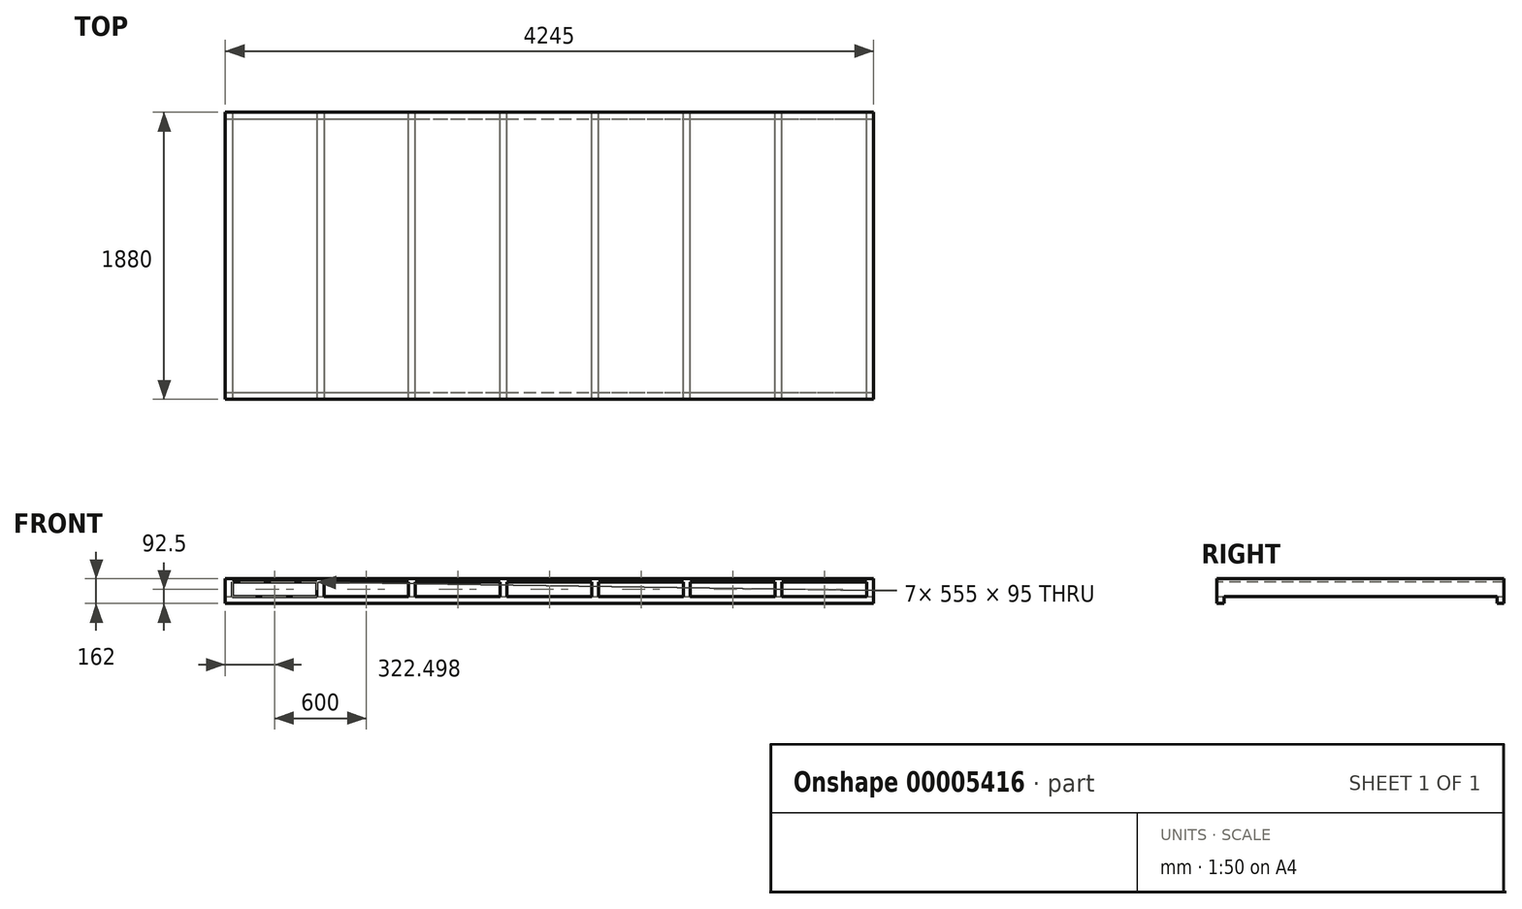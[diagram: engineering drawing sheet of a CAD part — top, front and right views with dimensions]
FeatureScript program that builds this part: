
annotation { "Feature Type Name" : "Feature", "Feature Type Description" : "" }
export const myFeature = defineFeature(function(context is Context, id is Id, definition is map)
    precondition{}
    {
        {
            var Q0;
            Q0=qCreatedBy(makeId("Top.planeOp"),FACE);
            var sketch = newSketch(context, id + "F0", { "sketchPlane" : qUnion([Q0])});
            skLineSegment(sketch, "E0.bottom", {"start": v(-2505.62, 1182.9) * mm, "end": v(1739.38, 1182.9) * mm});
            skLineSegment(sketch, "E0.top", {"start": v(-2505.62, -697.1) * mm, "end": v(1739.38, -697.1) * mm});
            skLineSegment(sketch, "E0.left", {"start": v(-2505.62, 1182.9) * mm, "end": v(-2505.62, -697.1) * mm});
            skLineSegment(sketch, "E0.right", {"start": v(1739.38, 1182.9) * mm, "end": v(1739.38, -697.1) * mm});
            skSolve(sketch);
        }
        {
            var Q0;
            Q0 = qSketchRegion(id + "F0", true);
            extrude(context, id + "F1", {"entities" : qUnion([Q0]), "depth" : 22 * mm});
        }
        {
            var Q0;
            Q0=makeQuery(id+"F1.opExtrude","CAP_FACE",FACE,{"disambiguationData":[OSD([sQuery(id+"F0.wireOp",EDGE,"E0.bottom"),sQuery(id+"F0.wireOp",EDGE,"E0.top"),sQuery(id+"F0.wireOp",EDGE,"E0.left"),sQuery(id+"F0.wireOp",EDGE,"E0.right")])],"isStart":true});
            var sketch = newSketch(context, id + "F2", { "sketchPlane" : qUnion([Q0])});
            skLineSegment(sketch, "E1.bottom", {"start": v(-1305.62, 697.1) * mm, "end": v(-1260.62, 697.1) * mm});
            skLineSegment(sketch, "E1.top", {"start": v(-1305.62, -1182.9) * mm, "end": v(-1260.62, -1182.9) * mm});
            skLineSegment(sketch, "E1.left", {"start": v(-1305.62, 697.1) * mm, "end": v(-1305.62, -1182.9) * mm});
            skLineSegment(sketch, "E1.right", {"start": v(-1260.62, 697.1) * mm, "end": v(-1260.62, -1182.9) * mm});
            skLineSegment(sketch, "E2.bottom", {"start": v(-705.62, 697.1) * mm, "end": v(-660.62, 697.1) * mm});
            skLineSegment(sketch, "E2.top", {"start": v(-705.62, -1182.9) * mm, "end": v(-660.62, -1182.9) * mm});
            skLineSegment(sketch, "E2.left", {"start": v(-705.62, 697.1) * mm, "end": v(-705.62, -1182.9) * mm});
            skLineSegment(sketch, "E2.right", {"start": v(-660.62, 697.1) * mm, "end": v(-660.62, -1182.9) * mm});
            skLineSegment(sketch, "E3.bottom", {"start": v(-105.62, 697.1) * mm, "end": v(-60.62, 697.1) * mm});
            skLineSegment(sketch, "E3.top", {"start": v(-105.62, -1182.9) * mm, "end": v(-60.62, -1182.9) * mm});
            skLineSegment(sketch, "E3.left", {"start": v(-105.62, 697.1) * mm, "end": v(-105.62, -1182.9) * mm});
            skLineSegment(sketch, "E3.right", {"start": v(-60.62, 697.1) * mm, "end": v(-60.62, -1182.9) * mm});
            skLineSegment(sketch, "E4.bottom", {"start": v(1739.38, 697.1) * mm, "end": v(1694.38, 697.1) * mm});
            skLineSegment(sketch, "E4.top", {"start": v(1739.38, -1182.9) * mm, "end": v(1694.38, -1182.9) * mm});
            skLineSegment(sketch, "E4.left", {"start": v(1739.38, 697.1) * mm, "end": v(1739.38, -1182.9) * mm});
            skLineSegment(sketch, "E4.right", {"start": v(1694.38, 697.1) * mm, "end": v(1694.38, -1182.9) * mm});
            skLineSegment(sketch, "E5.bottom", {"start": v(1139.38, 697.1) * mm, "end": v(1094.38, 697.1) * mm});
            skLineSegment(sketch, "E5.top", {"start": v(1139.38, -1182.9) * mm, "end": v(1094.38, -1182.9) * mm});
            skLineSegment(sketch, "E5.left", {"start": v(1139.38, 697.1) * mm, "end": v(1139.38, -1182.9) * mm});
            skLineSegment(sketch, "E5.right", {"start": v(1094.38, 697.1) * mm, "end": v(1094.38, -1182.9) * mm});
            skLineSegment(sketch, "E6.bottom", {"start": v(539.38, 697.1) * mm, "end": v(494.38, 697.1) * mm});
            skLineSegment(sketch, "E6.top", {"start": v(539.38, -1182.9) * mm, "end": v(494.38, -1182.9) * mm});
            skLineSegment(sketch, "E6.left", {"start": v(539.38, 697.1) * mm, "end": v(539.38, -1182.9) * mm});
            skLineSegment(sketch, "E6.right", {"start": v(494.38, 697.1) * mm, "end": v(494.38, -1182.9) * mm});
            skLineSegment(sketch, "E7.bottom", {"start": v(-1860.62, -1182.9) * mm, "end": v(-1905.62, -1182.9) * mm});
            skLineSegment(sketch, "E7.top", {"start": v(-1860.62, 697.1) * mm, "end": v(-1905.62, 697.1) * mm});
            skLineSegment(sketch, "E7.left", {"start": v(-1860.62, -1182.9) * mm, "end": v(-1860.62, 697.1) * mm});
            skLineSegment(sketch, "E7.right", {"start": v(-1905.62, -1182.9) * mm, "end": v(-1905.62, 697.1) * mm});
            skLineSegment(sketch, "E8.bottom", {"start": v(-2460.62, -1182.9) * mm, "end": v(-2505.62, -1182.9) * mm});
            skLineSegment(sketch, "E8.top", {"start": v(-2460.62, 697.1) * mm, "end": v(-2505.62, 697.1) * mm});
            skLineSegment(sketch, "E8.left", {"start": v(-2460.62, -1182.9) * mm, "end": v(-2460.62, 697.1) * mm});
            skLineSegment(sketch, "E8.right", {"start": v(-2505.62, -1182.9) * mm, "end": v(-2505.62, 697.1) * mm});
            skSolve(sketch);
        }
        {
            var Q0;
            Q0 = qSketchRegion(id + "F2", true);
            extrude(context, id + "F3", {"entities" : qUnion([Q0]), "operationType" : NewBodyOperationType.ADD, "depth" : 95 * mm});
        }
        {
            var Q0;
            Q0=makeQuery(id+"F3.opExtrude","CAP_FACE",FACE,{"disambiguationData":[OSD([sQuery(id+"F2.wireOp",EDGE,"E8.bottom"),sQuery(id+"F2.wireOp",EDGE,"E8.top"),sQuery(id+"F2.wireOp",EDGE,"E8.left"),sQuery(id+"F2.wireOp",EDGE,"E8.right")])],"isStart":false});
            var sketch = newSketch(context, id + "F4", { "sketchPlane" : qUnion([Q0])});
            skLineSegment(sketch, "E9.bottom", {"start": v(-2505.62, 697.1) * mm, "end": v(1739.38, 697.1) * mm});
            skLineSegment(sketch, "E9.top", {"start": v(-2505.62, 652.1) * mm, "end": v(1739.38, 652.1) * mm});
            skLineSegment(sketch, "E9.left", {"start": v(-2505.62, 697.1) * mm, "end": v(-2505.62, 652.1) * mm});
            skLineSegment(sketch, "E9.right", {"start": v(1739.38, 697.1) * mm, "end": v(1739.38, 652.1) * mm});
            skLineSegment(sketch, "E10.bottom", {"start": v(-2505.62, -1182.9) * mm, "end": v(1739.38, -1182.9) * mm});
            skLineSegment(sketch, "E10.top", {"start": v(-2505.62, -1137.9) * mm, "end": v(1739.38, -1137.9) * mm});
            skLineSegment(sketch, "E10.left", {"start": v(-2505.62, -1182.9) * mm, "end": v(-2505.62, -1137.9) * mm});
            skLineSegment(sketch, "E10.right", {"start": v(1739.38, -1182.9) * mm, "end": v(1739.38, -1137.9) * mm});
            skSolve(sketch);
        }
        {
            var Q0;
            Q0 = qSketchRegion(id + "F4", true);
            extrude(context, id + "F5", {"entities" : qUnion([Q0]), "operationType" : NewBodyOperationType.ADD, "depth" : 45 * mm});
        }
    });
